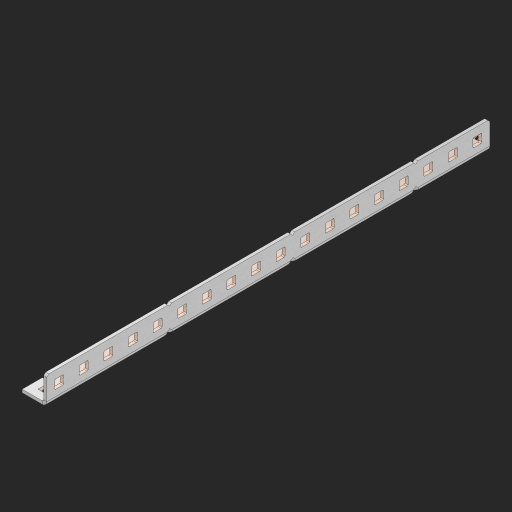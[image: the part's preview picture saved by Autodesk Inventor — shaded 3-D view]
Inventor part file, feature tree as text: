
AUTODESK INVENTOR PART (.ipt)
format: ipt  version: 2023 (Build 270158000, 158)  size: 933,376 bytes
history: native  units: in
note: dims shown in document units (in); Inventor stores cm internally (conversion verified against a paired STEP export)
features: other x202, extrude x52, sheet_metal_op x11, sketch x10, pattern_linear x2, mirror x1, chamfer x1
ambient origin geometry x8: Origin, YZ Plane, XZ Plane, XY Plane, X Axis, Y Axis, Z Axis, Center Point
bodies: Solid1 (feature_tree), Body (feature_tree)
feature tree (279):
  other  "Alu Half C 1x2x1x18"
  other  "Table"
  other  "Alu C 1x2x1x35"
  other  "Alu C 1x2x1x34"
  other  "Alu C 1x2x1x33"
  other  "Alu C 1x2x1x32"
  other  "Alu C 1x2x1x31"
  other  "Alu C 1x2x1x30"
  other  "Alu C 1x2x1x29"
  other  "Alu C 1x2x1x28"
  other  "Alu C 1x2x1x27"
  other  "Alu C 1x2x1x26"
  other  "Alu C 1x2x1x25"
  other  "Alu C 1x2x1x24"
  other  "Alu C 1x2x1x23"
  other  "Alu C 1x2x1x22"
  other  "Alu C 1x2x1x21"
  other  "Alu C 1x2x1x20"
  other  "Alu C 1x2x1x19"
  other  "Alu C 1x2x1x18"
  other  "Alu C 1x2x1x17"
  other  "Alu C 1x2x1x16"
  other  "Alu C 1x2x1x15"
  other  "Alu C 1x2x1x14"
  other  "Alu C 1x2x1x13"
  other  "Alu C 1x2x1x12"
  other  "Alu C 1x2x1x11"
  other  "Alu C 1x2x1x10"
  other  "Alu C 1x2x1x9"
  other  "Alu C 1x2x1x8"
  other  "Alu C 1x2x1x7"
  other  "Alu C 1x2x1x6"
  other  "Alu C 1x2x1x5"
  other  "Alu C 1x2x1x4"
  other  "Alu C 1x2x1x3"
  other  "Alu C 1x2x1x2"
  other  "Alu C 1x2x1x1"
  other  "Steel C 1x2x1x35"
  other  "Steel C 1x2x1x34"
  other  "Steel C 1x2x1x33"
  other  "Steel C 1x2x1x32"
  other  "Steel C 1x2x1x31"
  other  "Steel C 1x2x1x30"
  other  "Steel C 1x2x1x29"
  other  "Steel C 1x2x1x28"
  other  "Steel C 1x2x1x27"
  other  "Steel C 1x2x1x26"
  other  "Steel C 1x2x1x25"
  other  "Steel C 1x2x1x24"
  other  "Steel C 1x2x1x23"
  other  "Steel C 1x2x1x22"
  other  "Steel C 1x2x1x21"
  other  "Steel C 1x2x1x20"
  other  "Steel C 1x2x1x19"
  other  "Steel C 1x2x1x18"
  other  "Steel C 1x2x1x17"
  other  "Steel C 1x2x1x16"
  other  "Steel C 1x2x1x15"
  other  "Steel C 1x2x1x14"
  other  "Steel C 1x2x1x13"
  other  "Steel C 1x2x1x12"
  other  "Steel C 1x2x1x11"
  other  "Steel C 1x2x1x10"
  other  "Steel C 1x2x1x9"
  other  "Steel C 1x2x1x8"
  other  "Steel C 1x2x1x7"
  other  "Steel C 1x2x1x6"
  other  "Steel C 1x2x1x5"
  other  "Steel C 1x2x1x4"
  other  "Steel C 1x2x1x3"
  other  "Steel C 1x2x1x2"
  other  "Steel C 1x2x1x1"
  other  "Alu Half C 1x2x1x35"
  other  "Alu Half C 1x2x1x34"
  other  "Alu Half C 1x2x1x33"
  other  "Alu Half C 1x2x1x32"
  other  "Alu Half C 1x2x1x31"
  other  "Alu Half C 1x2x1x30"
  other  "Alu Half C 1x2x1x29"
  other  "Alu Half C 1x2x1x28"
  other  "Alu Half C 1x2x1x27"
  other  "Alu Half C 1x2x1x26"
  other  "Alu Half C 1x2x1x25"
  other  "Alu Half C 1x2x1x24"
  other  "Alu Half C 1x2x1x23"
  other  "Alu Half C 1x2x1x22"
  other  "Alu Half C 1x2x1x21"
  other  "Alu Half C 1x2x1x20"
  other  "Alu Half C 1x2x1x19"
  other  "Alu Half C 1x2x1x17"
  other  "Alu Half C 1x2x1x16"
  other  "Alu Half C 1x2x1x15"
  other  "Alu Half C 1x2x1x14"
  other  "Alu Half C 1x2x1x13"
  other  "Alu Half C 1x2x1x12"
  other  "Alu Half C 1x2x1x11"
  other  "Alu Half C 1x2x1x10"
  other  "Alu Half C 1x2x1x9"
  other  "Alu Half C 1x2x1x8"
  other  "Alu Half C 1x2x1x7"
  other  "Alu Half C 1x2x1x6"
  other  "Alu Half C 1x2x1x5"
  other  "Alu Half C 1x2x1x4"
  other  "Alu Half C 1x2x1x3"
  other  "Alu Half C 1x2x1x2"
  other  "Alu Half C 1x2x1x1"
  other  "Steel Half C 1x2x1x35"
  other  "Steel Half C 1x2x1x34"
  other  "Steel Half C 1x2x1x33"
  other  "Steel Half C 1x2x1x32"
  other  "Steel Half C 1x2x1x31"
  other  "Steel Half C 1x2x1x30"
  other  "Steel Half C 1x2x1x29"
  other  "Steel Half C 1x2x1x28"
  other  "Steel Half C 1x2x1x27"
  other  "Steel Half C 1x2x1x26"
  other  "Steel Half C 1x2x1x25"
  other  "Steel Half C 1x2x1x24"
  other  "Steel Half C 1x2x1x23"
  other  "Steel Half C 1x2x1x22"
  other  "Steel Half C 1x2x1x21"
  other  "Steel Half C 1x2x1x20"
  other  "Steel Half C 1x2x1x19"
  other  "Steel Half C 1x2x1x18"
  other  "Steel Half C 1x2x1x17"
  other  "Steel Half C 1x2x1x16"
  other  "Steel Half C 1x2x1x15"
  other  "Steel Half C 1x2x1x14"
  other  "Steel Half C 1x2x1x13"
  other  "Steel Half C 1x2x1x12"
  other  "Steel Half C 1x2x1x11"
  other  "Steel Half C 1x2x1x10"
  other  "Steel Half C 1x2x1x9"
  other  "Steel Half C 1x2x1x8"
  other  "Steel Half C 1x2x1x7"
  other  "Steel Half C 1x2x1x6"
  other  "Steel Half C 1x2x1x5"
  other  "Steel Half C 1x2x1x4"
  other  "Steel Half C 1x2x1x3"
  other  "Steel Half C 1x2x1x2"
  other  "Steel Half C 1x2x1x1"
  sheet_metal_op  "Flanges"
  other  "Flange Pattern Plane"
  other  "Flange Pattern Sketch"
  sheet_metal_op  "Flange Pattern"
  sheet_metal_op  "Body Pattern"
  pattern_linear  "Center Pattern"  Spacing1=0.0625in  [1 undecoded]
  other  "Arc Length"
  mirror  "Notch Mirror"
  pattern_linear  "Notch Pattern"  Spacing1=0.182in  [1 undecoded]
  chamfer  "End Chamfer"
  extrude  "Half Cut"  Depth=0.02in
  sketch  "Sketch1"  dims[d0=1.0in]
  other  "Plate1"
  sketch  "Sketch2"  dims[d1=9.0in]
  other  "Plate2"
  sheet_metal_op  "Bend1"
  sheet_metal_op  "Corner1"
  sketch  "Sketch3"  dims[d2=0.0625in]
  sketch  "Sketch7"  dims[d3=0.0625in]
  other  "Srf1"
  other  "Srf2"
  sketch  "Sketch8"  dims[d4=0.0312in]
  sketch  "Sketch9"  dims[d5=0.125in]
  other  "Srf91"
  sheet_metal_op  "Body Pattern Sketch"
  other  "Srf92"
  sketch  "Sketch13"  dims[d6=0.0625in]
  sketch  "Sketch14"  dims[d7=0.5in d8=90.0deg d9=0.0312in]
  sketch  "Sketch15"  dims[d10=0.25in]
  sketch  "Sketch16"  dims[d11=0.0625in d12=0.0625in d16=0.182in d17=0.02in d18=0.0625in d19=0.0in d20=0.25in d21=0.25in d38=7.0866in d40=0.5in d41=0.3937in d43=1.0in d46=0.172in d47=1.0in d48=0.0in d49=0.182in d50=0.02in d51=0.25in d52=0.25in d53=0.0625in d54=0.0in d55=0.172in d56=1.0in d57=0.0in d58=0.25in d60=7.0866in d62=0.5in d63=0.3937in d65=0.5in d85=0.1473in d86=0.1782in d88=0.04in d89=0.0625in d90=0.0in d91=0.04in d92=0.0491in d95=2.5in d96=0.04in d97=0.25in d98=45.0deg d99=0.25in d100=0.5in d101=0.0in d102=2.497in d106=0.182in d107=0.02in d108=0.5in d109=0.5in d110=0.0625in d111=0.0in d112=0.172in d113=0.5in d114=0.0in d117=0.5in d118=0.5in d119=0.5in]
  other  "Srf786"
  other  "Srf823"
  other  "Srf824"
  other  "Srf825"
  other  "Srf826"
  other  "Srf827"
  other  "Srf828"
  other  "Srf829"
  other  "Srf856"
  other  "Srf857"
  other  "Srf858"
  other  "Srf859"
  other  "Srf860"
  other  "Srf861"
  other  "Srf862"
  other  "Srf889"
  other  "Srf890"
  other  "Srf891"
  other  "Srf892"
  other  "Srf893"
  other  "Srf894"
  other  "Srf895"
  other  "Srf896"
  other  "Srf922"
  other  "Srf923"
  other  "Srf924"
  other  "Srf925"
  other  "Srf926"
  other  "Srf959"
  other  "Srf960"
  other  "Srf961"
  other  "Srf962"
  other  "Srf963"
  other  "Srf996"
  other  "Srf997"
  other  "Srf998"
  other  "Srf999"
  other  "Srf1000"
  other  "Srf1143"
  other  "Srf1144"
  other  "Srf1145"
  other  "Srf1146"
  other  "Srf1199"
  other  "Srf1200"
  other  "Srf1201"
  other  "Srf1202"
  other  "Srf1255"
  other  "Srf1256"
  other  "Srf1257"
  other  "Srf1258"
  sheet_metal_op  "Flange Stamp"
  sheet_metal_op  "Flange Circle"
  sheet_metal_op  "Body Stamp"
  sheet_metal_op  "Body Circle"
  other  "Center Stamp"
  other  "Center Circle"
  sheet_metal_op  "Notch"
  extrude  "ExtrusionSrf2"  Depth=0.0625in
  extrude  "ExtrusionSrf92"  TaperAngle=0.0deg  [1 undecoded]
  extrude  "ExtrusionSrf823"  Depth=0.25in
  extrude  "ExtrusionSrf824"  Depth=0.25in
  extrude  "ExtrusionSrf825"  Depth=0.5in
  extrude  "ExtrusionSrf826"  Depth=0.5in
  extrude  "ExtrusionSrf827"  Depth=1.0in TaperAngle=0.0deg
  extrude  "ExtrusionSrf828"  Depth=0.182in
  extrude  "ExtrusionSrf829"  Depth=0.02in
  extrude  "ExtrusionSrf856"  Depth=0.25in
  extrude  "ExtrusionSrf857"  Depth=0.25in
  extrude  "ExtrusionSrf858"  Depth=0.0625in
  extrude  "ExtrusionSrf859"  TaperAngle=0.0deg  [1 undecoded]
  extrude  "ExtrusionSrf860"  Depth=0.5in
  extrude  "ExtrusionSrf861"  Depth=1.0in TaperAngle=0.0deg
  extrude  "ExtrusionSrf862"  Depth=0.25in
  extrude  "ExtrusionSrf889"  Depth=0.5in
  extrude  "ExtrusionSrf890"  Depth=0.5in
  extrude  "ExtrusionSrf891"  Depth=0.5in
  extrude  "ExtrusionSrf892"  Depth=0.5in
  extrude  "ExtrusionSrf893"  Depth=0.5in
  extrude  "ExtrusionSrf894"  Depth=0.0625in
  extrude  "ExtrusionSrf895"  TaperAngle=0.0deg  [1 undecoded]
  extrude  "ExtrusionSrf896"  Depth=0.5in
  extrude  "ExtrusionSrf922"  Depth=0.5in
  extrude  "ExtrusionSrf923"  Depth=2.5in
  extrude  "ExtrusionSrf924"  Depth=0.25in TaperAngle=45.0deg
  extrude  "ExtrusionSrf925"  Depth=0.25in
  extrude  "ExtrusionSrf926"  Depth=0.5in TaperAngle=0.0deg
  extrude  "ExtrusionSrf959"  Depth=0.5in
  extrude  "ExtrusionSrf960"  Depth=0.182in
  extrude  "ExtrusionSrf961"  Depth=0.02in
  extrude  "ExtrusionSrf962"  Depth=0.5in
  extrude  "ExtrusionSrf963"  Depth=0.5in
  extrude  "ExtrusionSrf996"  Depth=0.0625in
  extrude  "ExtrusionSrf997"  TaperAngle=0.0deg  [1 undecoded]
  extrude  "ExtrusionSrf998"  Depth=0.5in
  extrude  "ExtrusionSrf999"  Depth=0.5in TaperAngle=0.0deg
  extrude  "ExtrusionSrf1000"  Depth=0.5in
  extrude  "ExtrusionSrf1143"  Depth=0.5in
  extrude  "ExtrusionSrf1144"  Depth=0.5in
  extrude  "ExtrusionSrf1145"  [1 undecoded]
  extrude  "ExtrusionSrf1146"  [1 undecoded]
  extrude  "ExtrusionSrf1199"  [1 undecoded]
  extrude  "ExtrusionSrf1200"  [1 undecoded]
  extrude  "ExtrusionSrf1201"  [1 undecoded]
  extrude  "ExtrusionSrf1202"  [1 undecoded]
  extrude  "ExtrusionSrf1255"  [1 undecoded]
  extrude  "ExtrusionSrf1256"  [1 undecoded]
  extrude  "ExtrusionSrf1257"  [1 undecoded]
  extrude  "ExtrusionSrf1258"  [1 undecoded]
note: 16 required parameter values undecoded (feature->parameter linkage not recoverable at this tier; creation-order binding heuristic only, values carry confidence <= 0.55)
